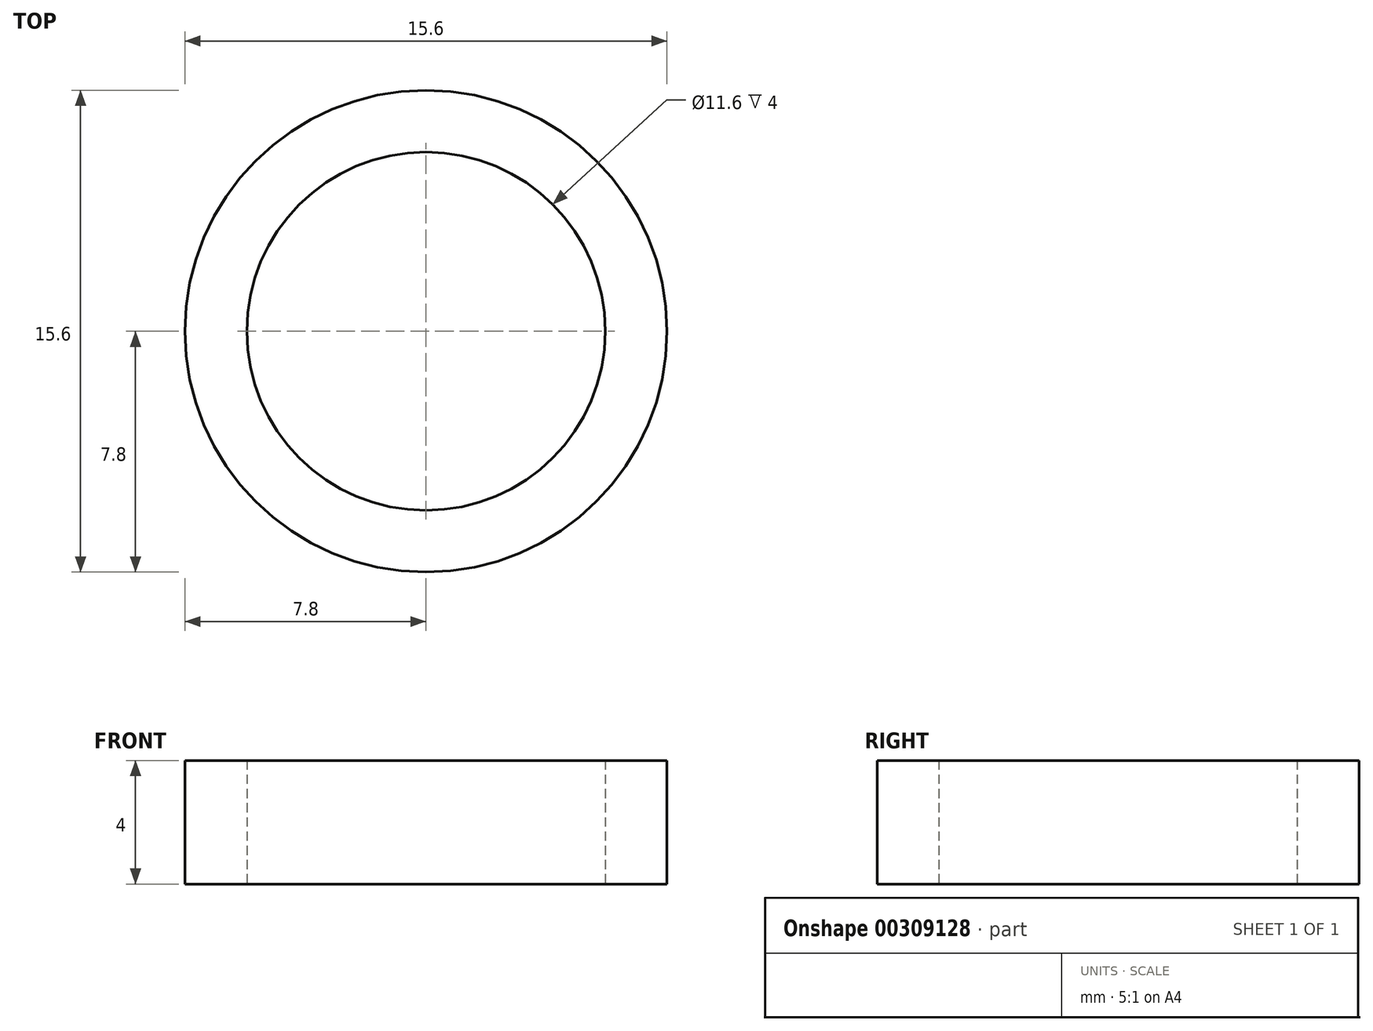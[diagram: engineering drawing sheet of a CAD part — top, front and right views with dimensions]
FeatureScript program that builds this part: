
annotation { "Feature Type Name" : "Feature", "Feature Type Description" : "" }
export const myFeature = defineFeature(function(context is Context, id is Id, definition is map)
    precondition{}
    {
        {
            var Q0;
            Q0=qCreatedBy(makeId("Top.planeOp"),FACE);
            var sketch = newSketch(context, id + "F0", { "sketchPlane" : qUnion([Q0])});
            skCircle(sketch, "E0", {"center": v(0, 0) * mm, "radius": 5.8 * mm});
            skCircle(sketch, "E1", {"center": v(0, 0) * mm, "radius": 7.8 * mm});
            skSolve(sketch);
        }
        {
            var Q0;
            Q0=makeQuery(id+"F0.imprint","IMPRINT",FACE,{"disambiguationData":[TD([[makeQuery(id+"F0.imprint","IMPRINT",EDGE,{"derivedFrom":sQuery(id+"F0.wireOp",EDGE,"E0")}),-1.0]])]});
            var Q1;
            Q1=sQuery(id+"F0.wireOp",EDGE,"E1");
            var Q2;
            Q2=sQuery(id+"F0.wireOp",EDGE,"E0");
            extrude(context, id + "F1", {"entities" : qUnion([Q0]), "surfaceEntities" : qUnion([Q1, Q2]), "depth" : 4 * mm});
        }
    });
